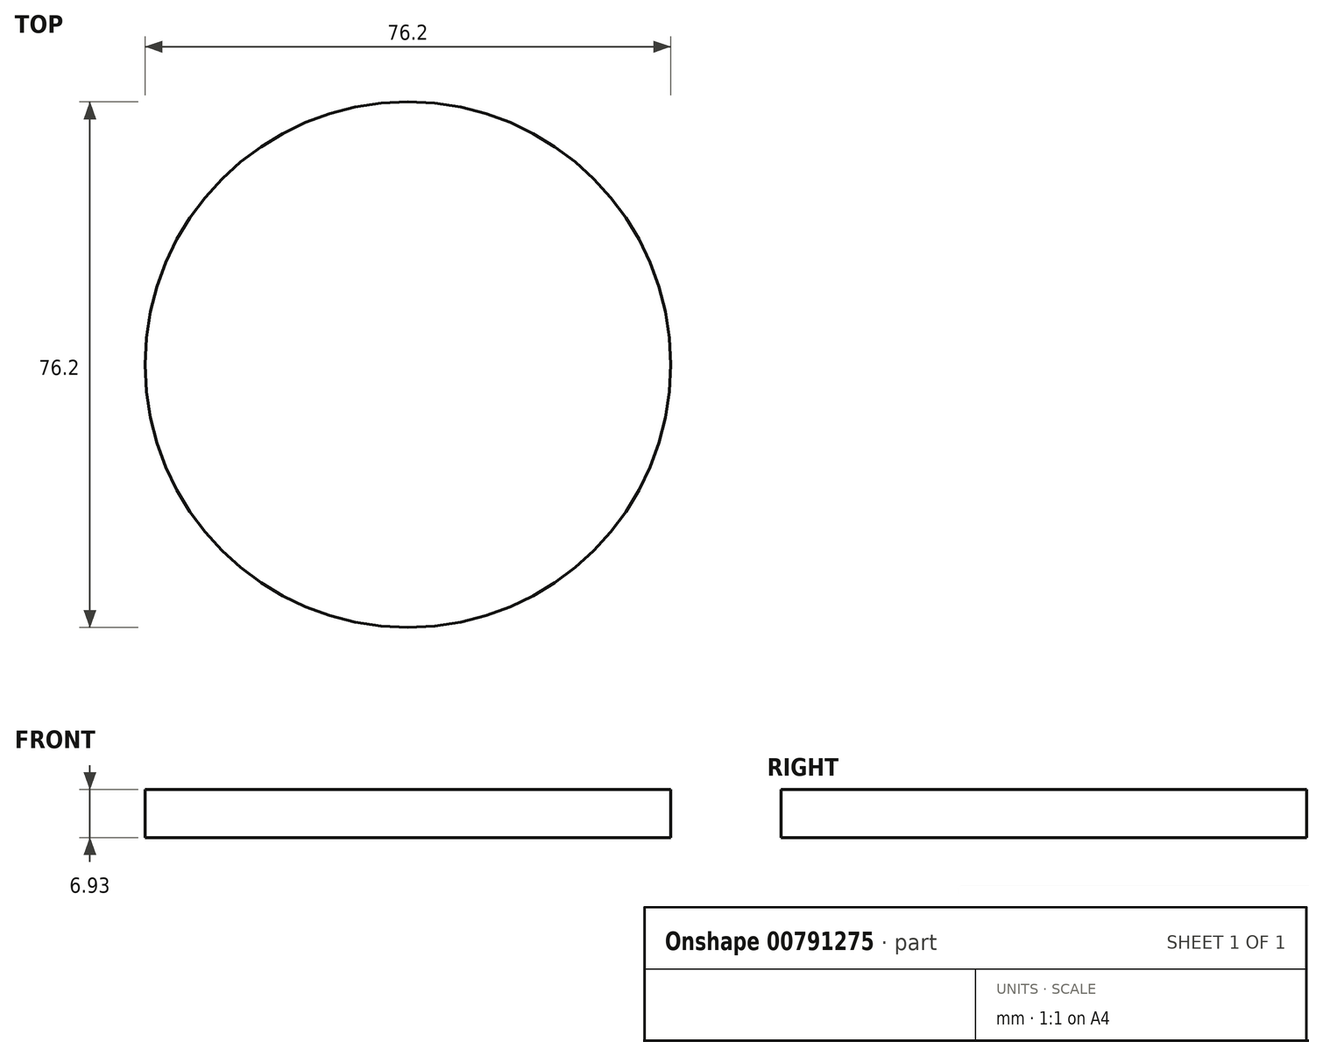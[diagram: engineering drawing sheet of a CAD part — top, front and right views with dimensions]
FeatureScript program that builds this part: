
annotation { "Feature Type Name" : "Feature", "Feature Type Description" : "" }
export const myFeature = defineFeature(function(context is Context, id is Id, definition is map)
    precondition{}
    {
        {
            var Q0;
            Q0=qCreatedBy(makeId("Top.planeOp"),FACE);
            var sketch = newSketch(context, id + "F0", { "sketchPlane" : qUnion([Q0])});
            skCircle(sketch, "E0", {"center": v(0, 0) * mm, "radius": 38.1 * mm});
            skSolve(sketch);
        }
        {
            var Q0;
            Q0 = qSketchRegion(id + "F0", true);
            extrude(context, id + "F1", {"entities" : qUnion([Q0]), "depth" : 6.93 * mm, "offsetDistance" : 25.4 * mm});
        }
    });
